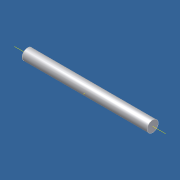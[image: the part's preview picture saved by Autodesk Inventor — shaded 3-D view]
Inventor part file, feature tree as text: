
AUTODESK INVENTOR PART (.ipt)
format: ipt  version: unknown  size: 156,672 bytes
history: native  units: mm
features: revolve x1, sketch x1
ambient origin geometry x8: Origin, YZ Plane, XZ Plane, XY Plane, X Axis, Y Axis, Z Axis, Center Point
feature tree (2):
  revolve  "Umdrehung1"
  sketch  "Skizze1"  dims[d0=1.4mm d1=31.7mm d2=90.0deg]
